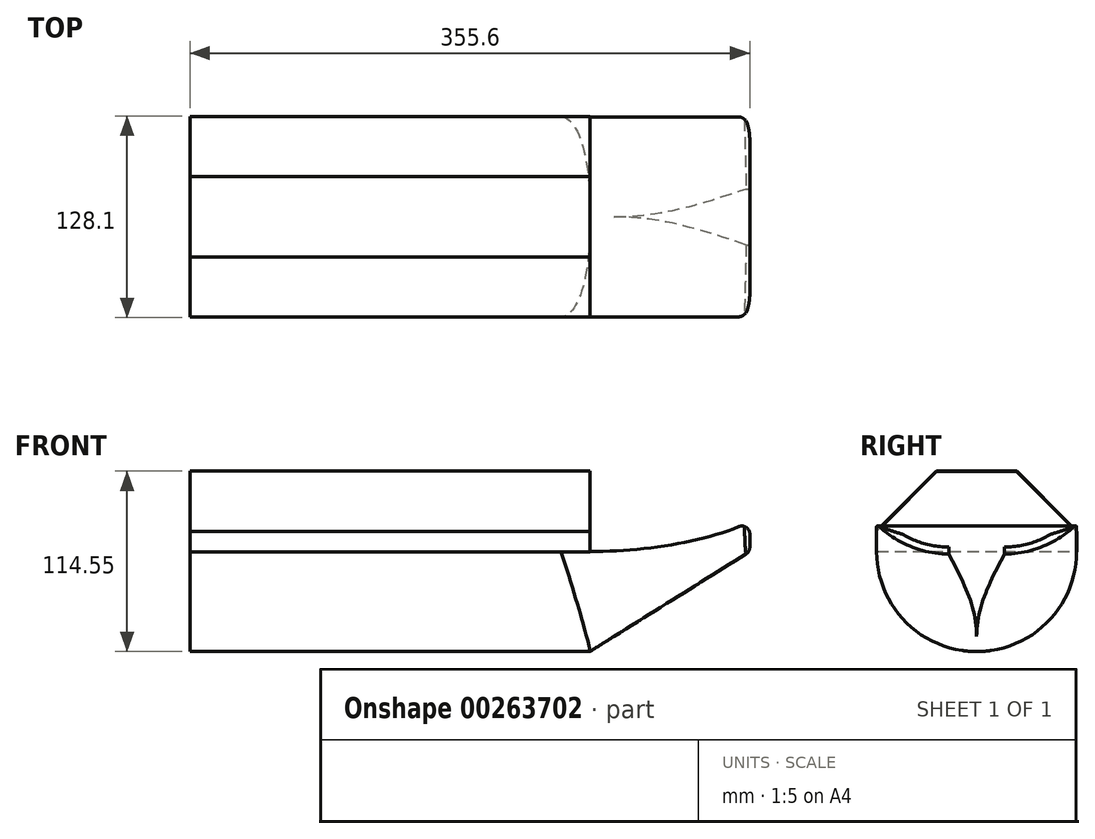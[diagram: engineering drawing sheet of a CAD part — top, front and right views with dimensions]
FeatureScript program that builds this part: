
annotation { "Feature Type Name" : "Feature", "Feature Type Description" : "" }
export const myFeature = defineFeature(function(context is Context, id is Id, definition is map)
    precondition{}
    {
        {
            var Q0;
            Q0=qCreatedBy(makeId("Front.planeOp"),FACE);
            var sketch = newSketch(context, id + "F0", { "sketchPlane" : qUnion([Q0])});
            skLineSegment(sketch, "E0.bottom", {"start": v(-127, 31.75) * mm, "end": v(127, 31.75) * mm});
            skLineSegment(sketch, "E0.top", {"start": v(-127, -31.75) * mm, "end": v(127, -31.75) * mm});
            skLineSegment(sketch, "E0.left", {"start": v(-127, 31.75) * mm, "end": v(-127, -31.75) * mm});
            skLineSegment(sketch, "E0.right", {"start": v(127, 31.75) * mm, "end": v(127, -31.75) * mm});
            skPoint(sketch, "E0.middle", {"position": v(0, 0) * mm});
            skLineSegment(sketch, "E1.top", {"start": v(-127, 82.55) * mm, "end": v(127, 82.55) * mm});
            skLineSegment(sketch, "E1.left", {"start": v(-127, 31.75) * mm, "end": v(-127, 82.55) * mm});
            skLineSegment(sketch, "E1.right", {"start": v(127, 31.75) * mm, "end": v(127, 82.55) * mm});
            skLineSegment(sketch, "E2.bottom", {"start": v(-127, 31.75) * mm, "end": v(-312.42, 31.75) * mm});
            skLineSegment(sketch, "E2.top", {"start": v(-127, 25.4) * mm, "end": v(-317.5, 25.4) * mm});
            skLineSegment(sketch, "E2.left", {"start": v(-127, 31.75) * mm, "end": v(-127, 25.4) * mm});
            skLineSegment(sketch, "E2.right", {"start": v(-317.5, 26.67) * mm, "end": v(-317.5, 25.4) * mm});
            skLineSegment(sketch, "E3", {"start": v(-228.6, 25.4) * mm, "end": v(-228.6, 8.38) * mm});
            skLineSegment(sketch, "E4", {"start": v(-207.88, -16.58) * mm, "end": v(-127, -31.75) * mm});
            skPoint(sketch, "E5.visualSharp", {"position": v(-228.6, -12.7) * mm});
            skArc(sketch, "E5.filletArc", {"start": v(-228.6, 8.38) * mm, "mid": v(-222.75, -7.84) * mm, "end": v(-207.88, -16.58) * mm});
            skPoint(sketch, "E6.visualSharp", {"position": v(-317.5, 31.75) * mm});
            skArc(sketch, "E6.filletArc", {"start": v(-312.42, 31.75) * mm, "mid": v(-316.01, 30.26) * mm, "end": v(-317.5, 26.67) * mm});
            skLineSegment(sketch, "E7", {"start": v(127, 31.75) * mm, "end": v(228.6, 31.75) * mm});
            skLineSegment(sketch, "E8", {"start": v(127, -31.75) * mm, "end": v(228.6, 31.75) * mm});
            skLineSegment(sketch, "E9", {"start": v(228.6, 31.75) * mm, "end": v(228.6, 50.8) * mm});
            skFitSpline(sketch, "E10", {"points": [v(127, 31.75) * mm, v(228.6, 50.8) * mm], "startDerivative": vector(104.07, 0) * mm, "endDerivative": vector(76.68, 38.6) * mm});
            skSolve(sketch);
        }
        {
            var Q0;
            Q0=makeQuery(id+"F0.imprint","IMPRINT",FACE,{"disambiguationData":[TD([[makeQuery(id+"F0.imprint","IMPRINT",EDGE,{"derivedFrom":sQuery(id+"F0.wireOp",EDGE,"E0.bottom")}),1.0]])]});
            extrude(context, id + "F1", {"entities" : qUnion([Q0]), "endBound" : BoundingType.SYMMETRIC, "depth" : 127 * mm});
        }
        {
            var Q0;
            Q0=makeQuery(id+"F1.opExtrude","CAP_EDGE",EDGE,{"disambiguationData":[OSD([sQuery(id+"F0.wireOp",EDGE,"E1.top")])],"isStart":false});
            var Q1;
            Q1=makeQuery(id+"F1.opExtrude","CAP_EDGE",EDGE,{"disambiguationData":[OSD([sQuery(id+"F0.wireOp",EDGE,"E1.top")])],"isStart":true});
            chamfer(context, id + "F2", {"entities" : qUnion([Q0, Q1]), "width" : 38.1 * mm, "tangentPropagation" : true});
        }
        {
            var Q0;
            Q0=makeQuery(id+"F1.opExtrude","SWEPT_FACE",FACE,{"disambiguationData":[OSD([sQuery(id+"F0.wireOp",EDGE,"E1.right")])]});
            var Q1;
            Q1=makeQuery(id+"F1.opExtrude","SWEPT_FACE",FACE,{"disambiguationData":[OSD([sQuery(id+"F0.wireOp",EDGE,"E1.left")])]});
            shell(context, id + "F3", {"entities" : qUnion([Q0, Q1]), "thickness" : 0.25 * mm, "oppositeDirection" : true});
        }
        {
            var Q0;
            Q0=makeQuery(id+"F0.imprint","IMPRINT",FACE,{"disambiguationData":[TD([[makeQuery(id+"F0.imprint","IMPRINT",EDGE,{"derivedFrom":sQuery(id+"F0.wireOp",EDGE,"E0.top")}),1.0]])]});
            extrude(context, id + "F4", {"entities" : qUnion([Q0]), "operationType" : NewBodyOperationType.ADD, "endBound" : BoundingType.SYMMETRIC, "depth" : 127 * mm});
        }
        {
            var Q0;
            Q0=makeQuery(id+"F4.opExtrude","CAP_EDGE",EDGE,{"disambiguationData":[OSD([sQuery(id+"F0.wireOp",EDGE,"E0.top")])],"isStart":false});
            var Q1;
            Q1=makeQuery(id+"F4.opExtrude","CAP_EDGE",EDGE,{"disambiguationData":[OSD([sQuery(id+"F0.wireOp",EDGE,"E0.top")])],"isStart":true});
            fillet(context, id + "F5", {"entities" : qUnion([Q0, Q1]), "radius" : 63.5 * mm, "tangentPropagation" : true, "allowEdgeOverflow" : false});
        }
        {
            var Q0;
            Q0=makeQuery(id+"F0.imprint","IMPRINT",FACE,{"disambiguationData":[TD([[makeQuery(id+"F0.imprint","IMPRINT",EDGE,{"derivedFrom":sQuery(id+"F0.wireOp",EDGE,"E0.right")}),1.0]])]});
            var Q1;
            Q1=makeQuery(id+"F0.imprint","IMPRINT",FACE,{"disambiguationData":[TD([[makeQuery(id+"F0.imprint","IMPRINT",EDGE,{"derivedFrom":sQuery(id+"F0.wireOp",EDGE,"E7")}),1.0]])]});
            extrude(context, id + "F6", {"entities" : qUnion([Q0, Q1]), "operationType" : NewBodyOperationType.ADD, "endBound" : BoundingType.SYMMETRIC, "depth" : 127 * mm});
        }
        {
            var Q0;
            Q0=makeQuery(id+"F6.opExtrude","CAP_EDGE",EDGE,{"disambiguationData":[OSD([sQuery(id+"F0.wireOp",EDGE,"E8")])],"isStart":false});
            var Q1;
            Q1=makeQuery(id+"F6.opExtrude","CAP_EDGE",EDGE,{"disambiguationData":[OSD([sQuery(id+"F0.wireOp",EDGE,"E8")])],"isStart":true});
            fillet(context, id + "F7", {"entities" : qUnion([Q0, Q1]), "radius" : 63.5 * mm, "tangentPropagation" : true, "allowEdgeOverflow" : false});
        }
        {
            var Q0;
            Q0=makeQuery(id+"F6.opExtrude","SWEPT_EDGE",EDGE,{"disambiguationData":[OSD([sQuery(id+"F0.wireOp",EDGE,"E9"),sQuery(id+"F0.wireOp",EDGE,"E10")])]});
            var Q1;
            {var subQ0=sQuery(id+"F0.wireOp",EDGE,"E8");Q1=makeQuery(id+"F7.opFillet","BLEND_EDGE",EDGE,{"disambiguationData":[OD(0.0)],"blendedFrom":[makeQuery(id+"F6.opExtrude","CAP_EDGE",EDGE,{"disambiguationData":[OSD([subQ0])],"isStart":true}),makeQuery(id+"F6.opExtrude","SWEPT_FACE",FACE,{"disambiguationData":[OSD([subQ0])]})],"blendedInto":[makeQuery(id+"F6.opExtrude","SWEPT_FACE",FACE,{"disambiguationData":[OSD([subQ0])]})]});}
            var Q2;
            {var subQ0=sQuery(id+"F0.wireOp",EDGE,"E8");Q2=makeQuery(id+"F7.opFillet","BLEND_EDGE",EDGE,{"disambiguationData":[OD(0.0)],"blendedFrom":[makeQuery(id+"F6.opExtrude","CAP_EDGE",EDGE,{"disambiguationData":[OSD([subQ0])],"isStart":false}),makeQuery(id+"F6.opExtrude","SWEPT_FACE",FACE,{"disambiguationData":[OSD([subQ0])]})],"blendedInto":[makeQuery(id+"F6.opExtrude","SWEPT_FACE",FACE,{"disambiguationData":[OSD([subQ0])]})]});}
            var Q3;
            Q3=makeQuery(id+"F6.opExtrude","SWEPT_EDGE",EDGE,{"disambiguationData":[OSD([sQuery(id+"F0.wireOp",EDGE,"E7"),sQuery(id+"F0.wireOp",EDGE,"E8"),sQuery(id+"F0.wireOp",EDGE,"E9")])]});
            var Q4;
            Q4=makeQuery(id+"F7.opFillet","BLEND_EDGE",EDGE,{"blendedFrom":[makeQuery(id+"F6.opExtrude","CAP_EDGE",EDGE,{"disambiguationData":[OSD([sQuery(id+"F0.wireOp",EDGE,"E8")])],"isStart":true}),makeQuery(id+"F6.opExtrude","SWEPT_FACE",FACE,{"disambiguationData":[OSD([sQuery(id+"F0.wireOp",EDGE,"E9")])]})],"blendedInto":[makeQuery(id+"F6.opExtrude","SWEPT_FACE",FACE,{"disambiguationData":[OSD([sQuery(id+"F0.wireOp",EDGE,"E9")])]})]});
            var Q5;
            Q5=makeQuery(id+"F7.opFillet","BLEND_EDGE",EDGE,{"blendedFrom":[makeQuery(id+"F6.opExtrude","CAP_EDGE",EDGE,{"disambiguationData":[OSD([sQuery(id+"F0.wireOp",EDGE,"E8")])],"isStart":false}),makeQuery(id+"F6.opExtrude","SWEPT_FACE",FACE,{"disambiguationData":[OSD([sQuery(id+"F0.wireOp",EDGE,"E9")])]})],"blendedInto":[makeQuery(id+"F6.opExtrude","SWEPT_FACE",FACE,{"disambiguationData":[OSD([sQuery(id+"F0.wireOp",EDGE,"E9")])]})]});
            var Q6;
            {var subQ0=sQuery(id+"F0.wireOp",EDGE,"E8");Q6=makeQuery(id+"F7.opFillet","BLEND_EDGE",EDGE,{"disambiguationData":[OD(1.0)],"blendedFrom":[makeQuery(id+"F6.opExtrude","CAP_EDGE",EDGE,{"disambiguationData":[OSD([subQ0])],"isStart":true}),makeQuery(id+"F6.opExtrude","SWEPT_FACE",FACE,{"disambiguationData":[OSD([subQ0])]})],"blendedInto":[makeQuery(id+"F6.opExtrude","SWEPT_FACE",FACE,{"disambiguationData":[OSD([subQ0])]})]});}
            var Q7;
            {var subQ0=sQuery(id+"F0.wireOp",EDGE,"E8");Q7=makeQuery(id+"F7.opFillet","BLEND_EDGE",EDGE,{"disambiguationData":[OD(1.0)],"blendedFrom":[makeQuery(id+"F6.opExtrude","CAP_EDGE",EDGE,{"disambiguationData":[OSD([subQ0])],"isStart":false}),makeQuery(id+"F6.opExtrude","SWEPT_FACE",FACE,{"disambiguationData":[OSD([subQ0])]})],"blendedInto":[makeQuery(id+"F6.opExtrude","SWEPT_FACE",FACE,{"disambiguationData":[OSD([subQ0])]})]});}
            fillet(context, id + "F8", {"entities" : qUnion([Q0, Q1, Q2, Q3, Q4, Q5, Q6, Q7]), "radius" : 5.08 * mm, "tangentPropagation" : true, "allowEdgeOverflow" : false});
        }
    });
